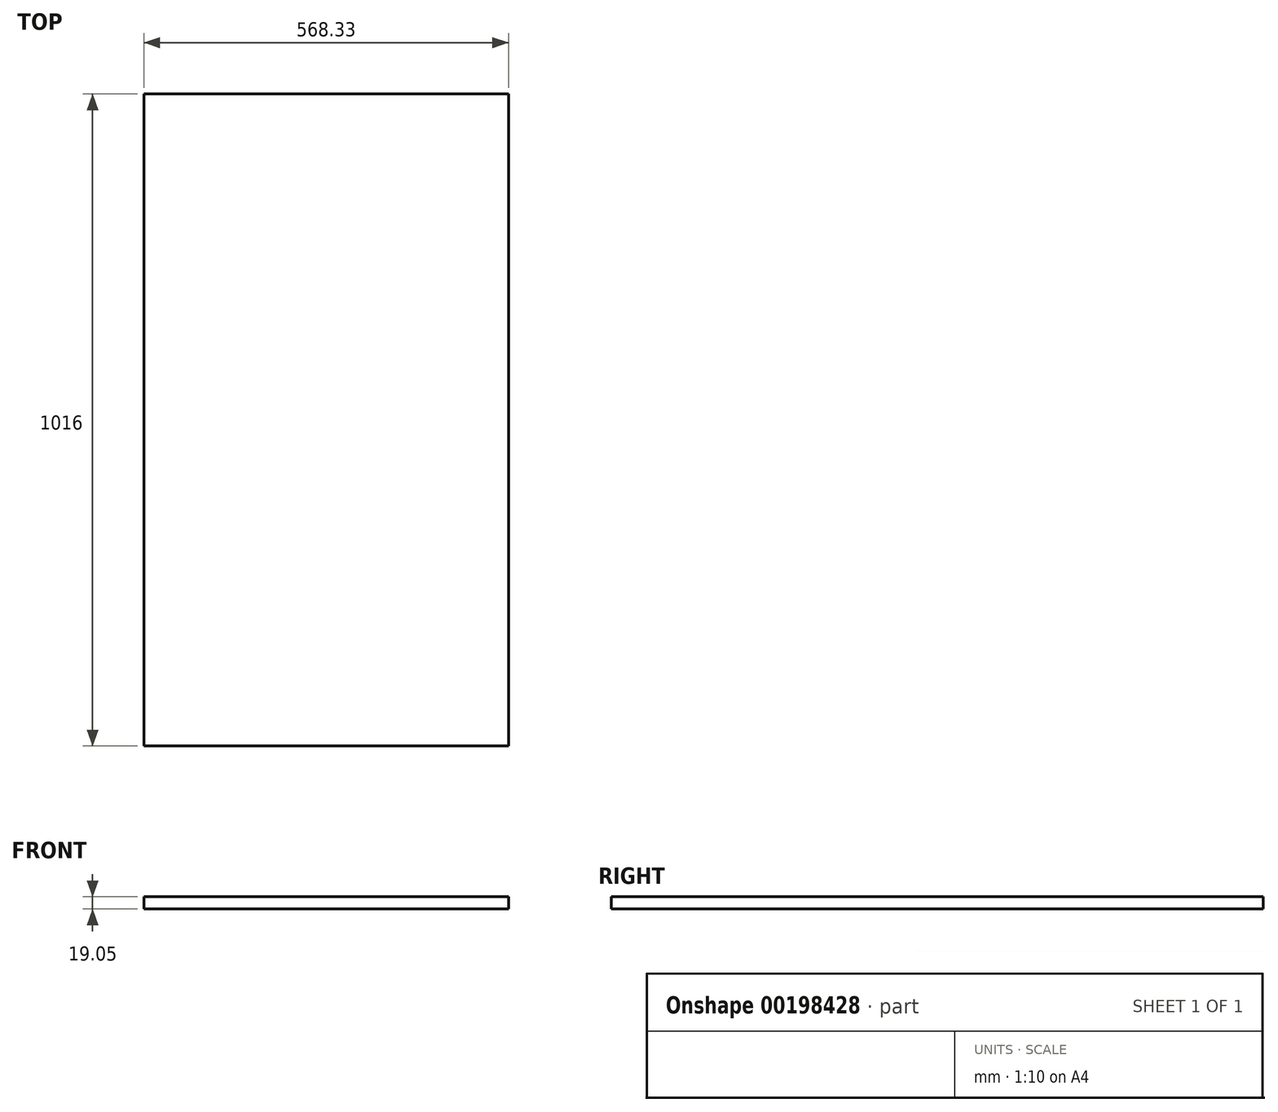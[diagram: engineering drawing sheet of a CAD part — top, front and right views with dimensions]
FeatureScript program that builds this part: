
annotation { "Feature Type Name" : "Feature", "Feature Type Description" : "" }
export const myFeature = defineFeature(function(context is Context, id is Id, definition is map)
    precondition{}
    {
        {
            var Q0;
            Q0=qCreatedBy(makeId("Top.planeOp"),FACE);
            var sketch = newSketch(context, id + "F0", { "sketchPlane" : qUnion([Q0])});
            skLineSegment(sketch, "E0.bottom", {"start": v(-301.49, -184.34) * mm, "end": v(266.84, -184.34) * mm});
            skLineSegment(sketch, "E0.top", {"start": v(-301.49, -1200.34) * mm, "end": v(266.84, -1200.34) * mm});
            skLineSegment(sketch, "E0.left", {"start": v(-301.49, -184.34) * mm, "end": v(-301.49, -1200.34) * mm});
            skLineSegment(sketch, "E0.right", {"start": v(266.84, -184.34) * mm, "end": v(266.84, -1200.34) * mm});
            skPoint(sketch, "E0.middle", {"position": v(-17.32, -692.34) * mm});
            skSolve(sketch);
        }
        {
            var Q0;
            Q0=makeQuery(id+"F0.imprint","IMPRINT",FACE,{"disambiguationData":[TD([[makeQuery(id+"F0.imprint","IMPRINT",EDGE,{"derivedFrom":sQuery(id+"F0.wireOp",EDGE,"E0.bottom")}),-1.0]])]});
            extrude(context, id + "F1", {"entities" : qUnion([Q0]), "depth" : 19.05 * mm});
        }
    });
